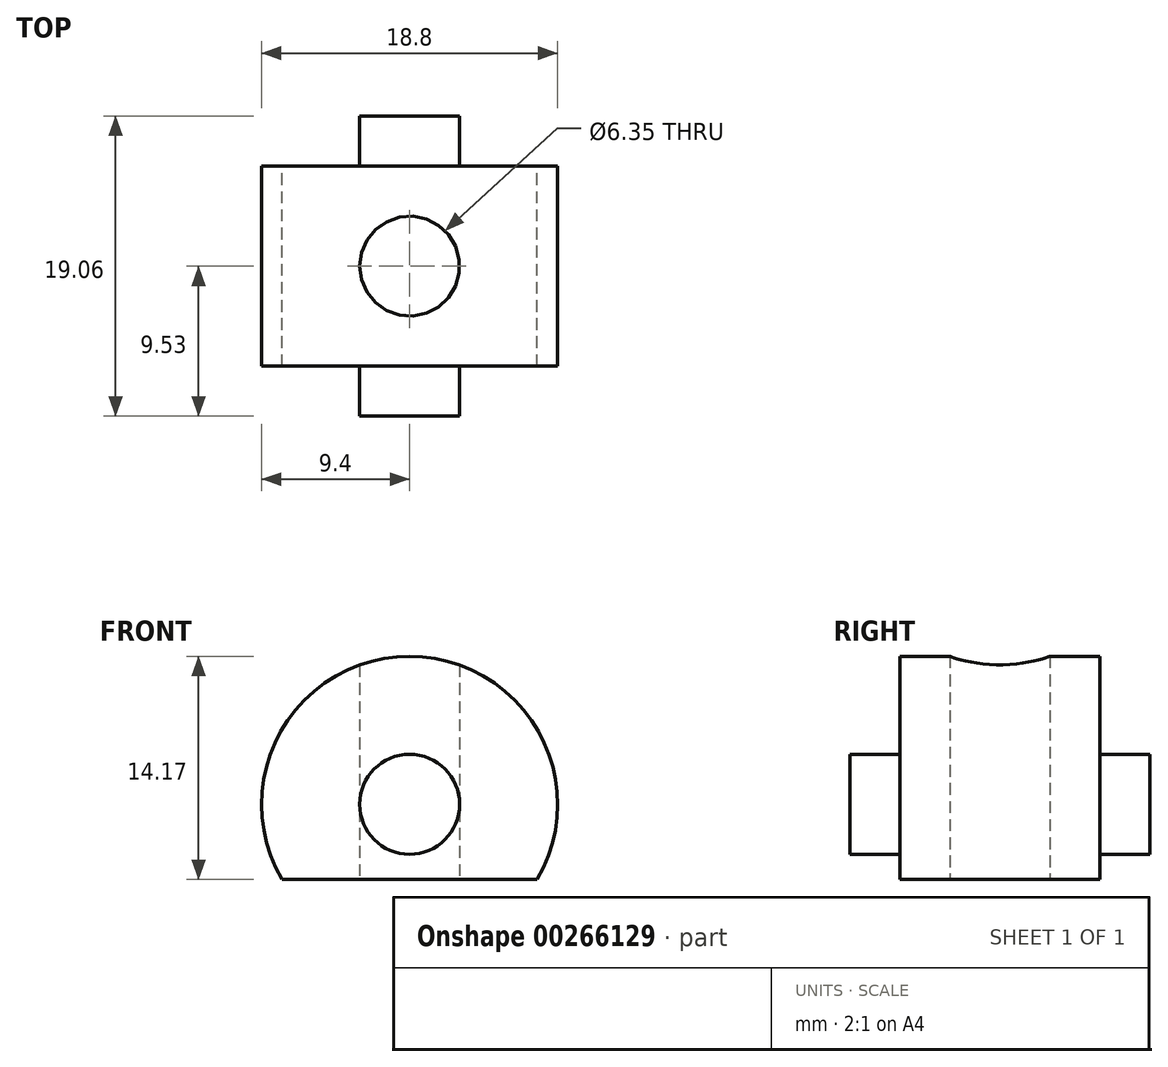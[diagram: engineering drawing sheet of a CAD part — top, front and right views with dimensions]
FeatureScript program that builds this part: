
annotation { "Feature Type Name" : "Feature", "Feature Type Description" : "" }
export const myFeature = defineFeature(function(context is Context, id is Id, definition is map)
    precondition{}
    {
        {
            var Q0;
            Q0=qCreatedBy(makeId("Front.planeOp"),FACE);
            var sketch = newSketch(context, id + "F0", { "sketchPlane" : qUnion([Q0])});
            skArc(sketch, "E0", {"start": v(8.1, -4.77) * mm, "mid": v(0, 9.4) * mm, "end": v(-8.1, -4.77) * mm});
            skLineSegment(sketch, "E1", {"start": v(-8.1, -4.77) * mm, "end": v(8.1, -4.77) * mm});
            skSolve(sketch);
        }
        {
            var Q0;
            Q0 = qSketchRegion(id + "F0", true);
            extrude(context, id + "F1", {"entities" : qUnion([Q0]), "depth" : 12.7 * mm});
        }
        {
            var Q0;
            Q0=makeQuery(id+"F1.opExtrude","CAP_FACE",FACE,{"disambiguationData":[OSD([sQuery(id+"F0.wireOp",EDGE,"E0"),sQuery(id+"F0.wireOp",EDGE,"E1")])],"isStart":false});
            var sketch = newSketch(context, id + "F2", { "sketchPlane" : qUnion([Q0])});
            skCircle(sketch, "E2", {"center": v(0, 0) * mm, "radius": 3.18 * mm});
            skSolve(sketch);
        }
        {
            var Q0;
            Q0 = qSketchRegion(id + "F2", true);
            extrude(context, id + "F3", {"entities" : qUnion([Q0]), "operationType" : NewBodyOperationType.ADD, "depth" : 3.17 * mm});
        }
        {
            var Q0;
            Q0=makeQuery(id+"F1.opExtrude","CAP_FACE",FACE,{"disambiguationData":[OSD([sQuery(id+"F0.wireOp",EDGE,"E0"),sQuery(id+"F0.wireOp",EDGE,"E1")])],"isStart":true});
            var sketch = newSketch(context, id + "F4", { "sketchPlane" : qUnion([Q0])});
            skCircle(sketch, "E3", {"center": v(0, 0) * mm, "radius": 3.18 * mm});
            skSolve(sketch);
        }
        {
            var Q0;
            Q0 = qSketchRegion(id + "F4", true);
            extrude(context, id + "F5", {"entities" : qUnion([Q0]), "operationType" : NewBodyOperationType.ADD, "depth" : 3.17 * mm});
        }
        {
            var Q0;
            Q0=makeQuery(id+"F1.opExtrude","SWEPT_FACE",FACE,{"disambiguationData":[OSD([sQuery(id+"F0.wireOp",EDGE,"E1")])]});
            var sketch = newSketch(context, id + "F6", { "sketchPlane" : qUnion([Q0])});
            skLineSegment(sketch, "E4", {"start": v(0, 0) * mm, "end": v(0, 12.7) * mm, "construction": true});
            skCircle(sketch, "E5", {"center": v(0, 6.35) * mm, "radius": 3.18 * mm});
            skSolve(sketch);
        }
        {
            var Q0;
            Q0 = qSketchRegion(id + "F6", true);
            extrude(context, id + "F7", {"entities" : qUnion([Q0]), "operationType" : NewBodyOperationType.REMOVE, "oppositeDirection" : true, "depth" : 25.4 * mm, "hasSecondDirection" : true, "secondDirectionOppositeDirection" : false, "secondDirectionDepth" : 25.4 * mm});
        }
    });
